# Revit family: a.txt
name_source: partatom
category: Pipe Accessories
revit_build: Autodesk Revit 2018 (Build: 20190510_1515(x64)
units: mm (PartAtom-declared; Revit-internal decimal feet)

## family parameters
Always vertical = Yes
Cut with Voids When Loaded = No
OmniClass Number = 23.65.00.00
OmniClass Title = Supply and Distribution of Liquids and Gases
Part Type = Normal
Round Connector Dimension = Use Diameter
Shared = No
Work Plane-Based = No

## types (1)
- Defauly - please load Revit Family Type Catalog
    3-Ways = No
    4-Ways = No
    A = 28 mm
    Antifreeze: = Passiveted Propylene Glycol
    Application fluids = Water or glycol solutions
    B = 38 mm  [stored 0.124672 ft]
    B1 = 38 mm  [stored 0.124672 ft]
    B2 = 38 mm  [stored 0.124672 ft]
    BIMobject category = Plumbing Valves
    Brand url = www.pintossi.it
    Conditioning: = as indicated by the producer
    Copper (CU): = < 0,1 mg/kg (< 0,05 mg/kg for steam)
    Description = Pintossi+C modular manifolds with obliqued valves are the perfect solutions to be used on hydralulic and heating systems.
The valves assebled on each outlet allow the regulation of the flow and the exclusion of the final device for maintanace works.
The ergonomic wheelhandle makes the opening/closing operation very easy.
Each manifolds is supplied with specific red and blue labels (hot and cold) for the correct designation of the outlet.
The sealing is guaranteed by PTM system (Pintossi soft sealing), which allow a quick and safe installation, without the use of additional sealing materials, like hemp of PTFE ribbon, which make possible a self-aligning connection.
    Design country = Italy
    E = 45 mm  [stored 0.147638 ft]
    Edition number = 0
    F = 62 mm
    Fluid aspect: = Limpid
    H = 89 mm  [stored 0.291995 ft]
    Hexagon Diameter = 29 mm
    I = 26 mm
    IFC Classification = Distribution Flow Element
    Inlet/Outlet Diameter = 24 mm  [stored 0.0787402 ft]
    Iron (FE): = < 0,5 mg/kg (< 0,1 mg/kg for steam)
    Main Inlet/Outlet Diameter = 19 mm
    Manufacturer = pintossi+C
    Manufacturer country = Italy
    Manufacturer name = Pintossi+C
    Masterformat 2014 Code = 35 20 12.19
    Masterformat 2014 Description = Hydraulic Manifolds
    Material Body = Pintossi - Metal - Brass Nickeled CW617N
    Material Cap Protection = Pintossi - Plastic - ABS
    Material Gaskets = Pintossi - Rubber - NBR
    Material main = Brass
    Maximum percentage of glycol [%] = 30
    Maximum working pressure = 10.0 bar
    Maximum working temperature = 100 °C
    Model = 3/4" x 24 x 19 - 2 ways - INT38
    NBS Reference Code = 55
    NBS Reference Description = Piped Supply Elements
    OmniClass Code = 23-39 21 13 21
    OmniClass Description = Manifolds
    PH: = Between 7 and 8
    Product Guid = 22ebe697-08f6-487b-a0da-4981bd81eda1
    Product SKU = 460-MODULAR-DISTRIBUTION-MANIFOLD-WITH-VALVES
    Product data url = https://www.bimobject.com
    Product family = MANIFOLDS
    Product group = LINEAR MANIFOLDS WITH VALVES
    QR code = https://www.bimobject.com
    Radius inner Main = 10 mm  [stored 0.0328084 ft]
    UNSPSC Code = 401416
    URL = www.pintossi.it
    Uniclass 1.4 Code = JS
    Uniclass 1.4 Description = Piped supply systems
    Uniclass 2.0 Code = EE-55
    Uniclass 2.0 Description = Piped Supply Elements
    Uniclass 2015 Code = Ss_55_70
    Uniclass 2015 Name = Water distribution and supply systems
    Uniformat II Code = D20
    Uniformat II Description = PLUMBING
    Weight Net (Kg) = 0

note: [stored X ft] marks values corroborated as IEEE doubles in the binary element streams (Revit-internal decimal feet)

## geometry (parser evidence)
native form markers: Sweep x2
no freeform markers — native parametric forms only
